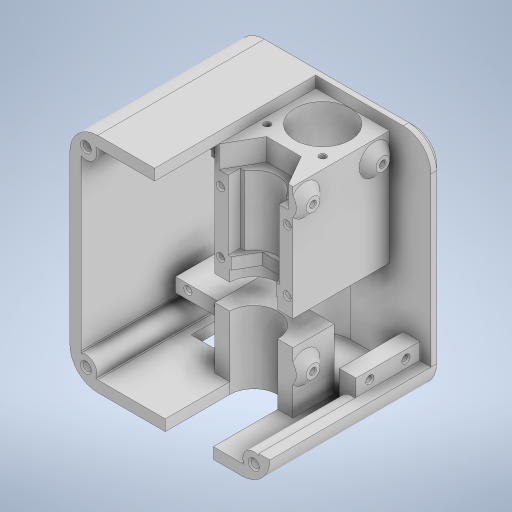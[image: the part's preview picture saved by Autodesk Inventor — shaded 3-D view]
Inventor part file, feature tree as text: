
AUTODESK INVENTOR PART (.ipt)
format: ipt  version: 2023 (Build 270158000, 158)  size: 723,968 bytes
history: native  units: mm
features: sketch x22, extrude x21, projected_geometry x6, chamfer x5, other x3, hole x2, fillet x1
ambient origin geometry x8: Origin, YZ Plane, XZ Plane, XY Plane, X Axis, Y Axis, Z Axis, Center Point
bodies: Body1 (feature_tree)
feature tree (60):
  other  "솔리드1"
  sketch  "스케치1"
  extrude  "돌출1"  Depth=20.0mm
  other  "작업 평면2"
  sketch  "스케치2"
  other  "작업 평면3"
  sketch  "스케치3"
  extrude  "돌출2"  Depth=54.0mm
  extrude  "돌출3"  Depth=40.0mm
  extrude  "돌출4"  Depth=48.0mm
  extrude  "돌출5"  Depth=11.0mm
  extrude  "돌출6"  Depth=2.0mm
  extrude  "돌출8"  Depth=20.0mm
  extrude  "돌출10"  Depth=18.0mm
  hole  "구멍1"  [1 undecoded]
  chamfer  "모따기1"  Distance=13.0mm
  sketch  "스케치12"
  extrude  "돌출14"  Depth=25.0mm
  fillet  "모깎기1"  Radius=13.3mm
  extrude  "돌출15"  Depth=9.95mm
  extrude  "돌출16"  Depth=24.0mm
  extrude  "돌출17"  Depth=16.0mm
  extrude  "돌출18"  Depth=4.5mm
  hole  "구멍2"  [1 undecoded]
  chamfer  "모따기2"  Distance=41.0mm
  sketch  "스케치21"
  extrude  "돌출19"  Depth=5.8mm
  extrude  "돌출20"  TaperAngle=0.0deg  [1 undecoded]
  extrude  "돌출21"  Depth=17.3mm
  extrude  "돌출22"  Depth=18.3mm
  chamfer  "모따기3"  Distance=8.5mm
  extrude  "돌출23"  Depth=8.0mm TaperAngle=0.0deg
  chamfer  "모따기4"  Distance=25.0mm
  extrude  "돌출24"  Depth=16.3mm
  chamfer  "모따기5"  Distance=4.2mm
  extrude  "돌출25"  Depth=17.3mm
  extrude  "돌출26"  Depth=35.0mm TaperAngle=0.0deg
  sketch  "스케치4"
  projected_geometry  "투영된 루프1"
  sketch  "스케치5"
  projected_geometry  "투영된 루프2"
  sketch  "스케치6"
  sketch  "스케치8"
  sketch  "스케치10"
  sketch  "스케치11"
  projected_geometry  "투영된 루프3"
  sketch  "스케치15"
  projected_geometry  "투영된 루프4"
  sketch  "스케치16"
  sketch  "스케치18"
  sketch  "스케치19"
  sketch  "스케치20"
  sketch  "스케치23"
  sketch  "스케치24"
  sketch  "스케치26"
  sketch  "스케치27"
  sketch  "스케치28"
  projected_geometry  "투영된 루프5"
  projected_geometry  "투영된 루프6"
  sketch  "스케치29"
note: 3 required parameter values undecoded (feature->parameter linkage not recoverable at this tier; creation-order binding heuristic only, values carry confidence <= 0.55)
